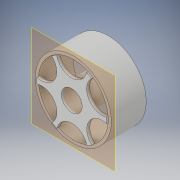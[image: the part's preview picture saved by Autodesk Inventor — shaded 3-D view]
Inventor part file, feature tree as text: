
AUTODESK INVENTOR PART (.ipt)
format: ipt  version: 2017 (Build 210142000, 142)  size: 162,304 bytes
history: native  units: in
note: dims shown in document units (in); Inventor stores cm internally (conversion verified against a paired STEP export)
features: extrude x3, sketch x3, projected_geometry x2, plane x1, pattern_circular x1
ambient origin geometry x8: Origin, YZ Plane, XZ Plane, XY Plane, X Axis, Y Axis, Z Axis, Center Point
bodies: Solid1 (feature_tree)
feature tree (10):
  extrude  "Extrusion1"  Depth=0.05in
  plane  "Work Plane1"
  extrude  "Extrusion2"  Depth=0.05in
  extrude  "Extrusion3"  TaperAngle=0.0deg  [1 undecoded]
  pattern_circular  "Circular Pattern1"  [2 undecoded]
  sketch  "Sketch1"  dims[d0=0.44in d1=0.05in]
  sketch  "Sketch2"  dims[d2=0.35in d3=0.05in]
  projected_geometry  "Projected Loop1"
  projected_geometry  "Projected Loop2"
  sketch  "Sketch3"  dims[d4=0.57in d5=0.0in d6=0.0in d7=0.05in d8=0.0in d9=0.5in d10=0.05in d11=0.0in d12=2.3622in d13=360.0deg]
note: 3 required parameter values undecoded (feature->parameter linkage not recoverable at this tier; creation-order binding heuristic only, values carry confidence <= 0.55)
